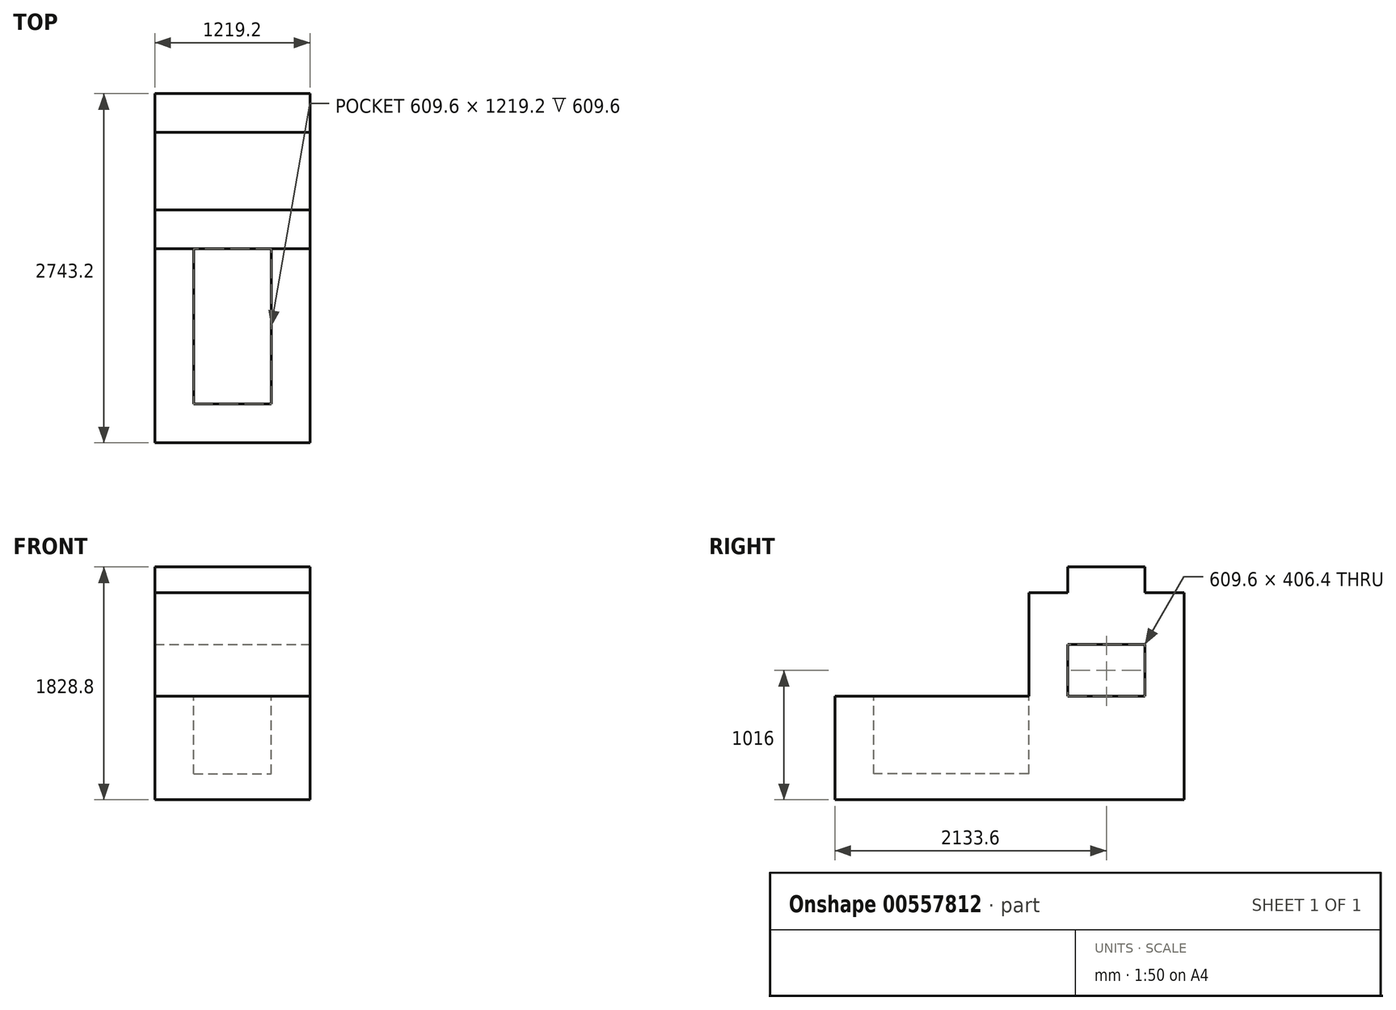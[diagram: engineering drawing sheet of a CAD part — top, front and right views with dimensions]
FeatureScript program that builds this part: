
annotation { "Feature Type Name" : "Feature", "Feature Type Description" : "" }
export const myFeature = defineFeature(function(context is Context, id is Id, definition is map)
    precondition{}
    {
        {
            var Q0;
            Q0=qCreatedBy(makeId("Right.planeOp"),FACE);
            var sketch = newSketch(context, id + "F0", { "sketchPlane" : qUnion([Q0])});
            skLineSegment(sketch, "E0", {"start": v(-66.16, -812.8) * mm, "end": v(-66.16, 0) * mm});
            skLineSegment(sketch, "E1", {"start": v(-66.16, 0) * mm, "end": v(1457.84, 0) * mm});
            skLineSegment(sketch, "E2", {"start": v(1457.84, 0) * mm, "end": v(1457.84, 812.8) * mm});
            skLineSegment(sketch, "E3", {"start": v(1457.84, 812.8) * mm, "end": v(1762.64, 812.8) * mm});
            skLineSegment(sketch, "E4", {"start": v(1762.64, 812.8) * mm, "end": v(1762.64, 1016) * mm});
            skLineSegment(sketch, "E5", {"start": v(1762.64, 1016) * mm, "end": v(2372.24, 1016) * mm});
            skLineSegment(sketch, "E6", {"start": v(2372.24, 1016) * mm, "end": v(2372.24, 812.8) * mm});
            skLineSegment(sketch, "E7", {"start": v(2372.24, 812.8) * mm, "end": v(2677.04, 812.8) * mm});
            skLineSegment(sketch, "E8", {"start": v(2677.04, 812.8) * mm, "end": v(2677.04, -812.8) * mm});
            skLineSegment(sketch, "E9", {"start": v(2677.04, -812.8) * mm, "end": v(-66.16, -812.8) * mm});
            skSolve(sketch);
        }
        {
            var Q0;
            Q0=makeQuery(id+"F0.imprint","IMPRINT",FACE,{"disambiguationData":[TD([[makeQuery(id+"F0.imprint","IMPRINT",EDGE,{"derivedFrom":sQuery(id+"F0.wireOp",EDGE,"E0")}),-1.0]])]});
            extrude(context, id + "F1", {"entities" : qUnion([Q0]), "oppositeDirection" : true, "depth" : 1219.2 * mm, "offsetDistance" : 25.4 * mm});
        }
        {
            var Q0;
            Q0=makeQuery(id+"F1.opExtrude","SWEPT_FACE",FACE,{"disambiguationData":[OSD([sQuery(id+"F0.wireOp",EDGE,"E1")])]});
            var sketch = newSketch(context, id + "F2", { "sketchPlane" : qUnion([Q0])});
            skLineSegment(sketch, "E10", {"start": v(-1219.2, 1457.84) * mm, "end": v(-914.4, 1457.84) * mm});
            skLineSegment(sketch, "E11", {"start": v(-914.4, 1457.84) * mm, "end": v(-914.4, 238.64) * mm});
            skLineSegment(sketch, "E12", {"start": v(-914.4, 238.64) * mm, "end": v(-304.8, 238.64) * mm});
            skLineSegment(sketch, "E13", {"start": v(-304.8, 238.64) * mm, "end": v(-304.8, 1457.84) * mm});
            skSolve(sketch);
        }
        {
            var Q0;
            {var subQ0=sQuery(id+"F2.wireOp",EDGE,"E11");Q0=makeQuery(id+"F2.imprint","IMPRINT",FACE,{"disambiguationData":[TD([[makeQuery(id+"F2.imprint","IMPRINT",EDGE,{"derivedFrom":subQ0}),1.0]])]});}
            extrude(context, id + "F3", {"entities" : qUnion([Q0]), "operationType" : NewBodyOperationType.REMOVE, "oppositeDirection" : true, "depth" : 609.6 * mm, "offsetDistance" : 25.4 * mm});
        }
        {
            var Q0;
            Q0=makeQuery(id+"F1.opExtrude","CAP_FACE",FACE,{"disambiguationData":[OSD([sQuery(id+"F0.wireOp",EDGE,"E0"),sQuery(id+"F0.wireOp",EDGE,"E1"),sQuery(id+"F0.wireOp",EDGE,"E2"),sQuery(id+"F0.wireOp",EDGE,"E3"),sQuery(id+"F0.wireOp",EDGE,"E4"),sQuery(id+"F0.wireOp",EDGE,"E5"),sQuery(id+"F0.wireOp",EDGE,"E6"),sQuery(id+"F0.wireOp",EDGE,"E7"),sQuery(id+"F0.wireOp",EDGE,"E8"),sQuery(id+"F0.wireOp",EDGE,"E9")])],"isStart":true});
            var sketch = newSketch(context, id + "F4", { "sketchPlane" : qUnion([Q0])});
            skLineSegment(sketch, "E14", {"start": v(1457.84, 0) * mm, "end": v(1762.64, 0) * mm});
            skLineSegment(sketch, "E15", {"start": v(1762.64, 0) * mm, "end": v(1762.64, 406.4) * mm});
            skLineSegment(sketch, "E16", {"start": v(1762.64, 406.4) * mm, "end": v(2372.24, 406.4) * mm});
            skLineSegment(sketch, "E17", {"start": v(2372.24, 406.4) * mm, "end": v(2372.24, 0) * mm});
            skLineSegment(sketch, "E18", {"start": v(2372.24, 0) * mm, "end": v(1762.64, 0) * mm});
            skSolve(sketch);
        }
        {
            var Q0;
            Q0=makeQuery(id+"F4.imprint","IMPRINT",FACE,{"disambiguationData":[TD([[makeQuery(id+"F4.imprint","IMPRINT",EDGE,{"derivedFrom":sQuery(id+"F4.wireOp",EDGE,"E15")}),-1.0]])]});
            extrude(context, id + "F5", {"entities" : qUnion([Q0]), "operationType" : NewBodyOperationType.REMOVE, "endBound" : BoundingType.THROUGH_ALL, "oppositeDirection" : true, "depth" : 25.4 * mm, "offsetDistance" : 25.4 * mm});
        }
    });
